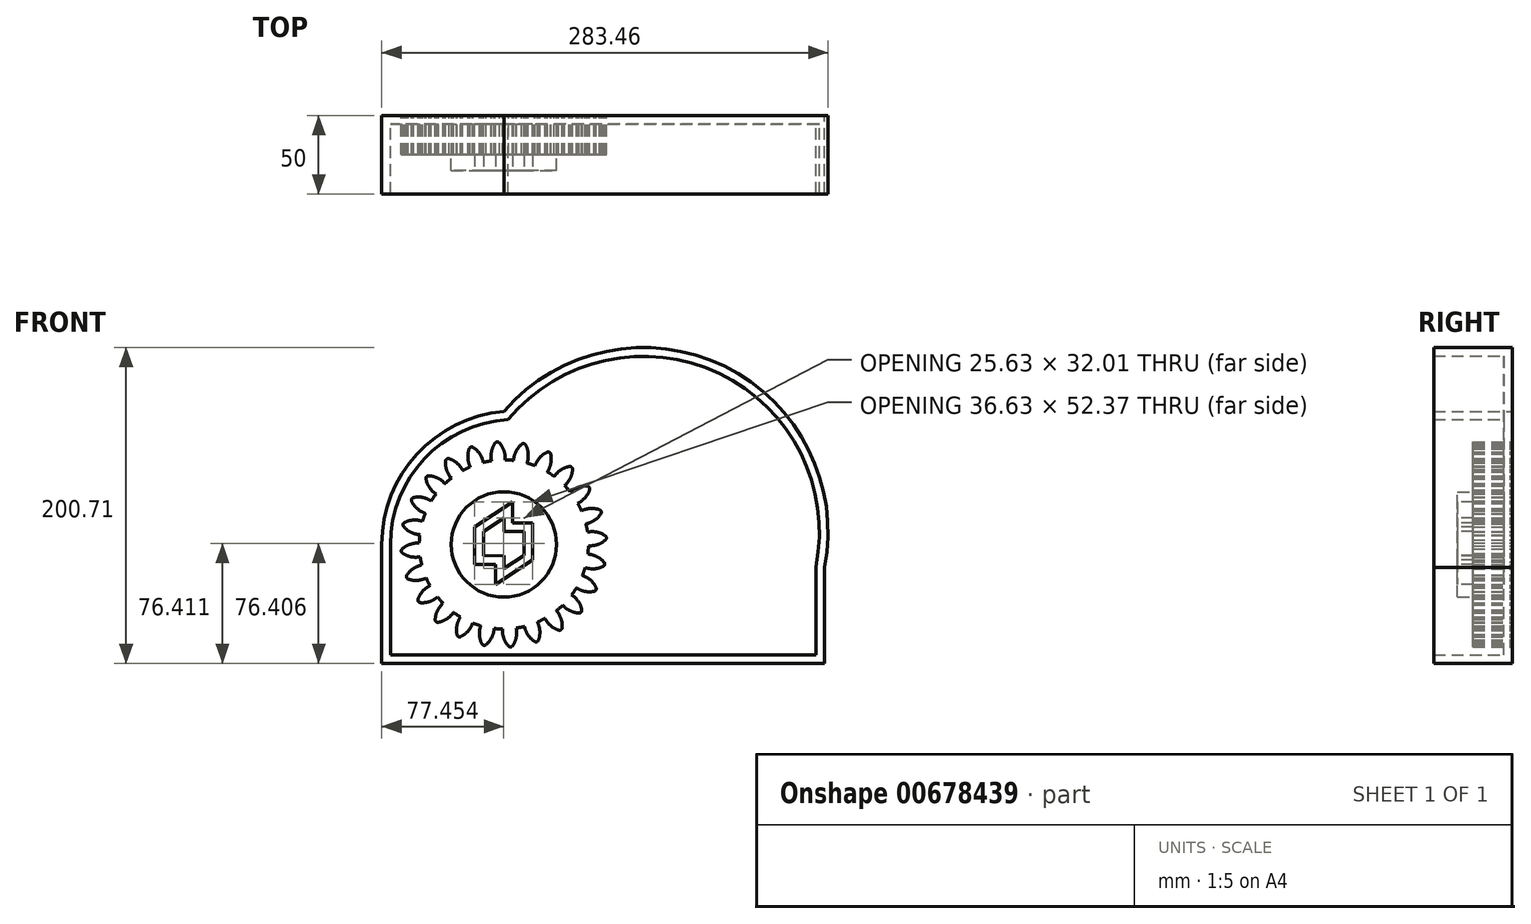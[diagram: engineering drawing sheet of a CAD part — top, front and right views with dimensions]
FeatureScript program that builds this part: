
annotation { "Feature Type Name" : "Feature", "Feature Type Description" : "" }
export const myFeature = defineFeature(function(context is Context, id is Id, definition is map)
    precondition{}
    {
        {
            var Q0;
            Q0=qCreatedBy(makeId("Front.planeOp"),FACE);
            var sketch = newSketch(context, id + "F0", { "sketchPlane" : qUnion([Q0])});
            skCircle(sketch, "E0", {"center": v(0, 1.08) * mm, "radius": 58.67 * mm, "construction": true});
            skCircle(sketch, "E1", {"center": v(0, 1.08) * mm, "radius": 63.5 * mm, "construction": true});
            skCircle(sketch, "E2", {"center": v(0, 0) * mm, "radius": 53.72 * mm});
            skLineSegment(sketch, "E3", {"start": v(0, 0) * mm, "end": v(-5.31, 81.05) * mm, "construction": true});
            skLineSegment(sketch, "E4", {"start": v(0, 59.76) * mm, "end": v(-52.82, 59.76) * mm, "construction": true});
            skLineSegment(sketch, "E5", {"start": v(0, 59.76) * mm, "end": v(-56.13, 39.33) * mm, "construction": true});
            skCircle(sketch, "E6", {"center": v(0, 1.08) * mm, "radius": 55.14 * mm, "construction": true});
            skCircle(sketch, "E7", {"center": v(0, 59.76) * mm, "radius": 14.6 * mm, "construction": true});
            skCircle(sketch, "E8", {"center": v(-13.72, 54.76) * mm, "radius": 14.6 * mm, "construction": true});
            skArc(sketch, "E9", {"start": v(0, 59.76) * mm, "mid": v(-1.2, 62.28) * mm, "end": v(-2.86, 64.52) * mm});
            skArc(sketch, "E10", {"start": v(0.84, 53.71) * mm, "mid": v(0.73, 56.78) * mm, "end": v(0, 59.76) * mm});
            skArc(sketch, "E11.MirrorCS", {"start": v(-7.8, 59.25) * mm, "mid": v(-6.95, 61.9) * mm, "end": v(-5.59, 64.34) * mm});
            skArc(sketch, "E12.MirrorCS", {"start": v(-7.85, 53.14) * mm, "mid": v(-8.13, 56.2) * mm, "end": v(-7.8, 59.25) * mm});
            skArc(sketch, "E13", {"start": v(-2.86, 64.52) * mm, "mid": v(-4.27, 65.13) * mm, "end": v(-5.59, 64.34) * mm});
            skCircle(sketch, "E14", {"center": v(0, 0) * mm, "radius": 33.45 * mm});
            skLineSegment(sketch, "E15", {"start": v(-10.16, 4.44) * mm, "end": v(-10.16, -3.9) * mm});
            skLineSegment(sketch, "E16", {"start": v(-10.16, -3.9) * mm, "end": v(9.22, -3.9) * mm});
            skLineSegment(sketch, "E17", {"start": v(9.22, -3.9) * mm, "end": v(9.22, 5.23) * mm});
            skLineSegment(sketch, "E18", {"start": v(9.22, 5.23) * mm, "end": v(-10.16, 5.23) * mm});
            skSolve(sketch);
        }
        {
            var Q0;
            {var subQ0=sQuery(id+"F0.wireOp",EDGE,"E2");var subQ1=makeQuery(id+"F0.imprint","INTERSECT",VERTEX,{"derivedFrom":[subQ0,sQuery(id+"F0.wireOp",EDGE,"E10")]});Q0=makeQuery(id+"F0.imprint","IMPRINT",FACE,{"disambiguationData":[TD([[makeQuery(id+"F0.imprint","IMPRINT",EDGE,{"disambiguationData":[TD([[subQ1,-1.0]])],"derivedFrom":subQ0}),1.0]])]});}
            var Q1;
            Q1=makeQuery(id+"F0.imprint","IMPRINT",FACE,{"disambiguationData":[TD([[makeQuery(id+"F0.imprint","IMPRINT",EDGE,{"derivedFrom":sQuery(id+"F0.wireOp",EDGE,"E9")}),1.0]])]});
            extrude(context, id + "F1", {"entities" : qUnion([Q0, Q1]), "depth" : 25 * mm, "offsetDistance" : 25 * mm});
        }
        {
            var Q0;
            Q0=makeQuery(id+"F1.opExtrude","SWEPT_BODY",BODY,{"disambiguationData":[OSD([sQuery(id+"F0.wireOp",EDGE,"E2"),sQuery(id+"F0.wireOp",EDGE,"E9"),sQuery(id+"F0.wireOp",EDGE,"E10"),sQuery(id+"F0.wireOp",EDGE,"E11.MirrorCS"),sQuery(id+"F0.wireOp",EDGE,"E12.MirrorCS"),sQuery(id+"F0.wireOp",EDGE,"E13")])]});
            var Q1;
            Q1=makeQuery(id+"F1.opExtrude","SWEPT_FACE",FACE,{"disambiguationData":[OSD([sQuery(id+"F0.wireOp",EDGE,"E2")])]});
            circularPattern(context, id + "F2", {"entities" : qUnion([Q0]), "axis" : qUnion([Q1]), "angle" : 360 * degree, "instanceCount" : 24, "equalSpace" : true});
        }
        {
            var Q0;
            Q0=makeQuery(id+"F0.imprint","IMPRINT",FACE,{"disambiguationData":[TD([[makeQuery(id+"F0.imprint","IMPRINT",EDGE,{"derivedFrom":sQuery(id+"F0.wireOp",EDGE,"E14")}),1.0]])]});
            extrude(context, id + "F3", {"entities" : qUnion([Q0]), "operationType" : NewBodyOperationType.ADD, "depth" : 35 * mm, "offsetDistance" : 25 * mm});
        }
        {
            var Q0;
            Q0=qCreatedBy(makeId("Front.planeOp"),FACE);
            var sketch = newSketch(context, id + "F4", { "sketchPlane" : qUnion([Q0])});
            skLineSegment(sketch, "E19", {"start": v(-77.58, -75.67) * mm, "end": v(203.7, -75.67) * mm});
            skLineSegment(sketch, "E20", {"start": v(203.7, -75.67) * mm, "end": v(203.7, -14.7) * mm});
            skLineSegment(sketch, "E21", {"start": v(-77.58, -75.67) * mm, "end": v(-77.58, 0) * mm});
            skArc(sketch, "E22", {"start": v(0, 84.55) * mm, "mid": v(-55.24, 57.37) * mm, "end": v(-77.58, 0) * mm});
            skArc(sketch, "E23", {"start": v(203.7, -14.7) * mm, "mid": v(140, 113.2) * mm, "end": v(0, 84.55) * mm});
            skLineSegment(sketch, "E24", {"start": v(-12.94, 8.16) * mm, "end": v(-12.94, -7.16) * mm});
            skLineSegment(sketch, "E25", {"start": v(-12.94, 8.16) * mm, "end": v(12.7, 8.16) * mm});
            skLineSegment(sketch, "E26", {"start": v(12.7, 8.16) * mm, "end": v(12.7, -6.97) * mm});
            skLineSegment(sketch, "E27", {"start": v(12.7, -6.97) * mm, "end": v(-12.94, -7.16) * mm});
            skLineSegment(sketch, "E28", {"start": v(-12.94, 8.16) * mm, "end": v(0.16, 16.75) * mm});
            skLineSegment(sketch, "E29", {"start": v(0.16, 16.75) * mm, "end": v(0.16, 8.16) * mm});
            skLineSegment(sketch, "E30", {"start": v(12.7, -6.97) * mm, "end": v(0.16, -15.26) * mm});
            skLineSegment(sketch, "E31", {"start": v(0.16, -15.26) * mm, "end": v(0.1, -6.97) * mm});
            skSolve(sketch);
        }
        {
            var Q0;
            Q0=makeQuery(id+"F4.imprint","IMPRINT",FACE,{"disambiguationData":[TD([[makeQuery(id+"F4.imprint","IMPRINT",EDGE,{"derivedFrom":sQuery(id+"F4.wireOp",EDGE,"E19")}),1.0]])]});
            extrude(context, id + "F5", {"entities" : qUnion([Q0]), "depth" : 50 * mm, "offsetDistance" : 25 * mm});
        }
        {
            var Q0;
            Q0=makeQuery(id+"F5.opExtrude","CAP_FACE",FACE,{"disambiguationData":[OSD([sQuery(id+"F4.wireOp",EDGE,"E19"),sQuery(id+"F4.wireOp",EDGE,"E20"),sQuery(id+"F4.wireOp",EDGE,"E21"),sQuery(id+"F4.wireOp",EDGE,"E22"),sQuery(id+"F4.wireOp",EDGE,"E23")])],"isStart":false});
            shell(context, id + "F6", {"entities" : qUnion([Q0]), "thickness" : 5.5 * mm});
        }
        {
            var Q0;
            Q0=makeQuery(id+"F5.opExtrude","CAP_FACE",FACE,{"disambiguationData":[OSD([sQuery(id+"F4.wireOp",EDGE,"E19"),sQuery(id+"F4.wireOp",EDGE,"E20"),sQuery(id+"F4.wireOp",EDGE,"E21"),sQuery(id+"F4.wireOp",EDGE,"E22"),sQuery(id+"F4.wireOp",EDGE,"E23"),sQuery(id+"F4.wireOp",EDGE,"9bb9cda8-d9cf-4f2b-b52a-9fae2bf4f1f8.bottom"),sQuery(id+"F4.wireOp",EDGE,"9bb9cda8-d9cf-4f2b-b52a-9fae2bf4f1f8.top"),sQuery(id+"F4.wireOp",EDGE,"9bb9cda8-d9cf-4f2b-b52a-9fae2bf4f1f8.left"),sQuery(id+"F4.wireOp",EDGE,"9bb9cda8-d9cf-4f2b-b52a-9fae2bf4f1f8.right"),sQuery(id+"F4.wireOp",EDGE,"007c8448-b403-471b-90a4-4efc7fc63cd1"),sQuery(id+"F4.wireOp",EDGE,"96632b59-29c3-48de-8d53-52b4dfbf231e"),sQuery(id+"F4.wireOp",EDGE,"6a6df5ca-d6f7-4e33-afa7-ef7cb83a55e0"),sQuery(id+"F4.wireOp",EDGE,"6d5e69cf-d1e0-426c-b6ce-ce7c397284b1")])],"isStart":false});
            extrude(context, id + "F7", {"entities" : qUnion([Q0]), "operationType" : NewBodyOperationType.REMOVE, "oppositeDirection" : true, "depth" : 25 * mm, "offsetDistance" : 25 * mm});
        }
    });
